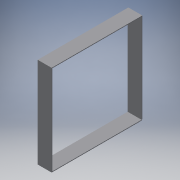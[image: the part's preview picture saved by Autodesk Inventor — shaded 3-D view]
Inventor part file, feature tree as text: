
AUTODESK INVENTOR PART (.ipt)
format: ipt  version: 2019 (Build 230136000, 136)  size: 122,880 bytes
history: native  units: in
note: dims shown in document units (in); Inventor stores cm internally (conversion verified against a paired STEP export)
features: extrude x4, sketch x4, other x3, reference x2, projected_geometry x1
ambient origin geometry x8: Origin, YZ Plane, XZ Plane, XY Plane, X Axis, Y Axis, Z Axis, Center Point
bodies: Solid1 (feature_tree)
feature tree (14):
  extrude  "Extrusion1"  Depth=15.0in
  extrude  "Extrusion2"  Depth=0.75in TaperAngle=0.0deg
  extrude  "Extrusion3"  Depth=0.75in TaperAngle=0.0deg
  extrude  "Extrusion4"  [1 undecoded]
  sketch  "Sketch1"  dims[d0=96.0in d1=15.0in]
  sketch  "Sketch2"  dims[d2=0.75in d3=0.0in d4=0.75in d5=0.0in]
  reference  "Reference1"
  sketch  "Sketch3"  dims[d6=0.75in d7=0.0in d8=0.75in d9=0.0in]
  reference  "Reference2"
  sketch  "Sketch4"
  projected_geometry  "Projected Loop1"
  other  "<userpath>\Desktop\Roombotics\RoomboticsField2018.iam"
  other  "RoomboticsField2018.iam"
  other  "Base:1"
note: 1 required parameter value undecoded (feature->parameter linkage not recoverable at this tier; creation-order binding heuristic only, values carry confidence <= 0.55)
